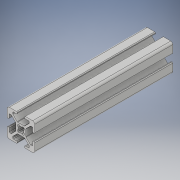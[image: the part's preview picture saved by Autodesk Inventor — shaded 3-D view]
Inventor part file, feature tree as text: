
AUTODESK INVENTOR PART (.ipt)
format: ipt  version: 2019 (Build 230136000, 136)  size: 239,616 bytes
history: native  units: mm
features: extrude x1, sketch x1
ambient origin geometry x8: Origin, YZ Plane, XZ Plane, XY Plane, X Axis, Y Axis, Z Axis, Center Point
bodies: Solid1 (feature_tree)
feature tree (2):
  extrude  "Extrusion1"  [1 undecoded]
  sketch  "Sketch_1"  dims[d0=100.25mm d1=0.0mm]
note: 1 required parameter value undecoded (feature->parameter linkage not recoverable at this tier; creation-order binding heuristic only, values carry confidence <= 0.55)
